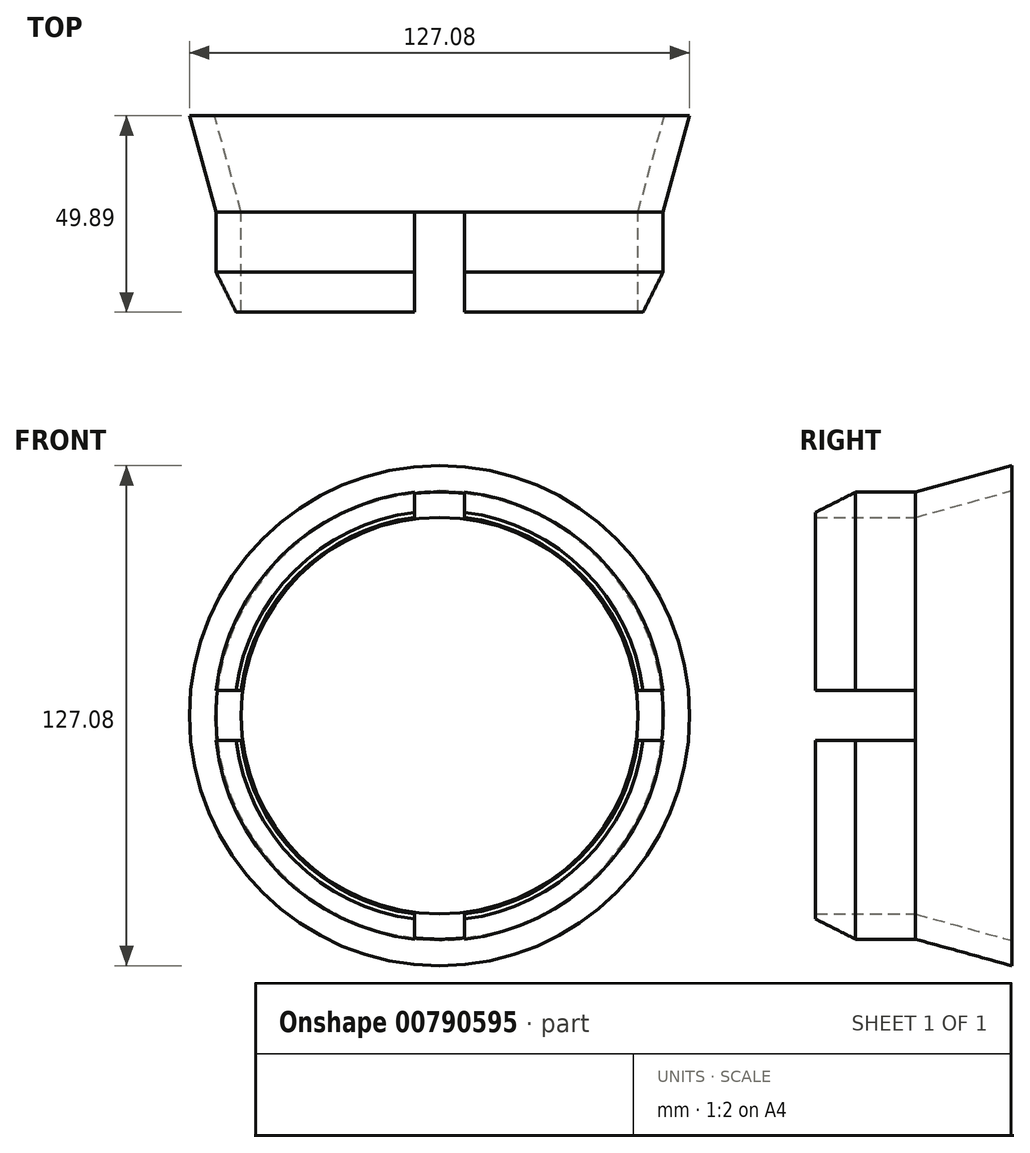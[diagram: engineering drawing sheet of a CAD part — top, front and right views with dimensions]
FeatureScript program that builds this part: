
annotation { "Feature Type Name" : "Feature", "Feature Type Description" : "" }
export const myFeature = defineFeature(function(context is Context, id is Id, definition is map)
    precondition{}
    {
        {
            var Q0;
            Q0=qCreatedBy(makeId("Front.planeOp"),FACE);
            var sketch = newSketch(context, id + "F0", { "sketchPlane" : qUnion([Q0])});
            skCircle(sketch, "E0", {"center": v(0, 0) * mm, "radius": 50.8 * mm});
            skCircle(sketch, "E1", {"center": v(0, 0) * mm, "radius": 57.15 * mm});
            skLineSegment(sketch, "E2", {"start": v(6.35, 56.8) * mm, "end": v(6.35, 50.4) * mm});
            skLineSegment(sketch, "E3", {"start": v(-6.35, 56.8) * mm, "end": v(-6.35, 50.4) * mm});
            skLineSegment(sketch, "E4", {"start": v(56.8, 6.35) * mm, "end": v(50.4, 6.35) * mm});
            skLineSegment(sketch, "E5", {"start": v(56.8, -6.35) * mm, "end": v(50.4, -6.35) * mm});
            skLineSegment(sketch, "E6", {"start": v(6.35, -56.8) * mm, "end": v(6.35, -50.4) * mm});
            skLineSegment(sketch, "E7", {"start": v(-6.35, -56.8) * mm, "end": v(-6.35, -50.4) * mm});
            skLineSegment(sketch, "E8", {"start": v(-56.8, 6.35) * mm, "end": v(-50.4, 6.35) * mm});
            skLineSegment(sketch, "E9", {"start": v(-56.8, -6.35) * mm, "end": v(-50.4, -6.35) * mm});
            skSolve(sketch);
        }
        {
            var Q0;
            {var subQ0=sQuery(id+"F0.wireOp",EDGE,"E3");Q0=makeQuery(id+"F0.imprint","IMPRINT",FACE,{"disambiguationData":[TD([[makeQuery(id+"F0.imprint","IMPRINT",EDGE,{"derivedFrom":subQ0}),-1.0]])]});}
            var Q1;
            {var subQ0=sQuery(id+"F0.wireOp",EDGE,"E2");Q1=makeQuery(id+"F0.imprint","IMPRINT",FACE,{"disambiguationData":[TD([[makeQuery(id+"F0.imprint","IMPRINT",EDGE,{"derivedFrom":subQ0}),1.0]])]});}
            var Q2;
            {var subQ0=sQuery(id+"F0.wireOp",EDGE,"E5");Q2=makeQuery(id+"F0.imprint","IMPRINT",FACE,{"disambiguationData":[TD([[makeQuery(id+"F0.imprint","IMPRINT",EDGE,{"derivedFrom":subQ0}),1.0]])]});}
            var Q3;
            {var subQ0=sQuery(id+"F0.wireOp",EDGE,"E7");Q3=makeQuery(id+"F0.imprint","IMPRINT",FACE,{"disambiguationData":[TD([[makeQuery(id+"F0.imprint","IMPRINT",EDGE,{"derivedFrom":subQ0}),1.0]])]});}
            extrude(context, id + "F1", {"entities" : qUnion([Q0, Q1, Q2, Q3]), "depth" : 25.4 * mm, "offsetDistance" : 25.4 * mm});
        }
        {
            var Q0;
            Q0=qCreatedBy(makeId("Right.planeOp"),FACE);
            var sketch = newSketch(context, id + "F2", { "sketchPlane" : qUnion([Q0])});
            skLineSegment(sketch, "E10", {"start": v(0, 56.8) * mm, "end": v(24.49, 63.54) * mm});
            skLineSegment(sketch, "E11", {"start": v(0, 50.4) * mm, "end": v(24.49, 57.15) * mm});
            skLineSegment(sketch, "E12", {"start": v(24.49, 63.54) * mm, "end": v(24.49, 57.15) * mm});
            skLineSegment(sketch, "E13", {"start": v(0, 56.8) * mm, "end": v(0, 50.4) * mm});
            skLineSegment(sketch, "E14", {"start": v(0, 0) * mm, "end": v(27.1, 0) * mm});
            skSolve(sketch);
        }
        {
            var Q0;
            Q0=makeQuery(id+"F2.imprint","IMPRINT",FACE,{"disambiguationData":[TD([[makeQuery(id+"F2.imprint","IMPRINT",EDGE,{"derivedFrom":sQuery(id+"F2.wireOp",EDGE,"E10")}),-1.0]])]});
            var Q1;
            Q1=sQuery(id+"F2.wireOp",EDGE,"E14");
            revolve(context, id + "F3", {"surfaceOperationType" : NewSurfaceOperationType.NEW, "entities" : qUnion([Q0]), "axis" : qUnion([Q1]), "revolveType" : RevolveType.FULL});
        }
        {
            var Q0;
            {var subQ0=sQuery(id+"F0.wireOp",EDGE,"E1");Q0=makeQuery(id+"F1.opExtrude","CAP_EDGE",EDGE,{"disambiguationData":[OSD([subQ0]),TDD([makeQuery(id+"F0.imprint","IMPRINT",EDGE,{"disambiguationData":[TD([[makeQuery(id+"F0.imprint","INTERSECT",VERTEX,{"derivedFrom":[subQ0,sQuery(id+"F0.wireOp",EDGE,"E2")]}),1.0]])],"derivedFrom":subQ0})])],"isStart":false});}
            var Q1;
            {var subQ0=sQuery(id+"F0.wireOp",EDGE,"E1");Q1=makeQuery(id+"F1.opExtrude","CAP_EDGE",EDGE,{"disambiguationData":[OSD([subQ0]),TDD([makeQuery(id+"F0.imprint","IMPRINT",EDGE,{"disambiguationData":[TD([[makeQuery(id+"F0.imprint","INTERSECT",VERTEX,{"derivedFrom":[subQ0,sQuery(id+"F0.wireOp",EDGE,"E3")]}),-1.0]])],"derivedFrom":subQ0})])],"isStart":false});}
            var Q2;
            {var subQ0=sQuery(id+"F0.wireOp",EDGE,"E1");Q2=makeQuery(id+"F1.opExtrude","CAP_EDGE",EDGE,{"disambiguationData":[OSD([subQ0]),TDD([makeQuery(id+"F0.imprint","IMPRINT",EDGE,{"disambiguationData":[TD([[makeQuery(id+"F0.imprint","INTERSECT",VERTEX,{"derivedFrom":[subQ0,sQuery(id+"F0.wireOp",EDGE,"E7")]}),1.0]])],"derivedFrom":subQ0})])],"isStart":false});}
            var Q3;
            {var subQ0=sQuery(id+"F0.wireOp",EDGE,"E1");Q3=makeQuery(id+"F1.opExtrude","CAP_EDGE",EDGE,{"disambiguationData":[OSD([subQ0]),TDD([makeQuery(id+"F0.imprint","IMPRINT",EDGE,{"disambiguationData":[TD([[makeQuery(id+"F0.imprint","INTERSECT",VERTEX,{"derivedFrom":[subQ0,sQuery(id+"F0.wireOp",EDGE,"E5")]}),1.0]])],"derivedFrom":subQ0})])],"isStart":false});}
            chamfer(context, id + "F4", {"entities" : qUnion([Q0, Q1, Q2, Q3]), "chamferType" : ChamferType.TWO_OFFSETS, "width1" : 5.08 * mm, "oppositeDirection" : false, "width2" : 10.16 * mm, "tangentPropagation" : true});
        }
    });
